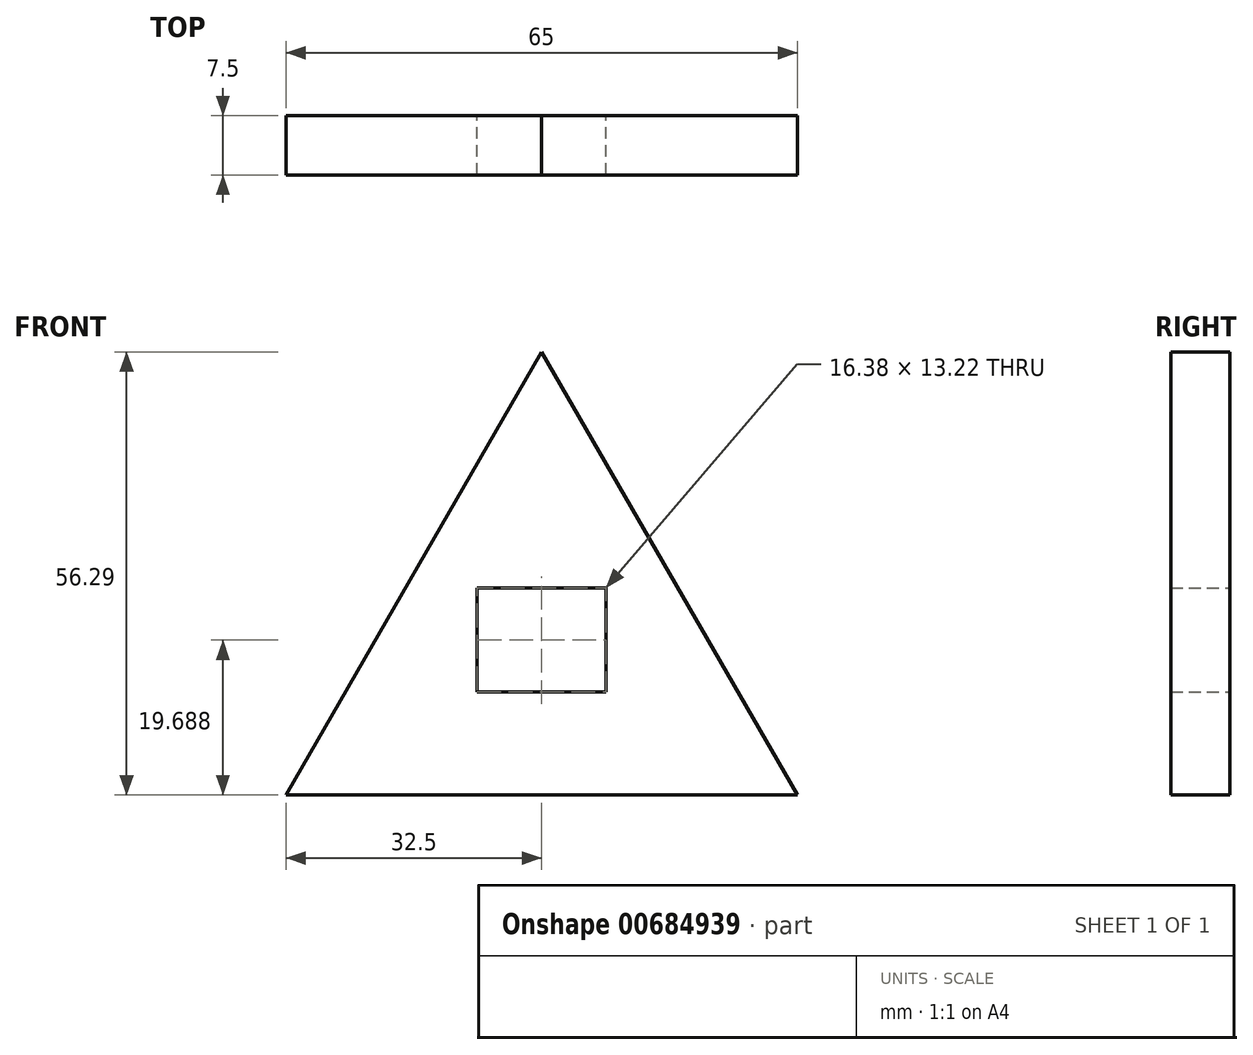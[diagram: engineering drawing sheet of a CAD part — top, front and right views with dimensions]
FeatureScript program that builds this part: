
annotation { "Feature Type Name" : "Feature", "Feature Type Description" : "" }
export const myFeature = defineFeature(function(context is Context, id is Id, definition is map)
    precondition{}
    {
        {
            var Q0;
            Q0=qCreatedBy(makeId("Front.planeOp"),FACE);
            var sketch = newSketch(context, id + "F0", { "sketchPlane" : qUnion([Q0])});
            skLineSegment(sketch, "E0", {"start": v(0, 56.3) * mm, "end": v(-32.5, 0) * mm});
            skLineSegment(sketch, "E1", {"start": v(-32.5, 0) * mm, "end": v(32.5, 0) * mm});
            skLineSegment(sketch, "E2", {"start": v(32.5, 0) * mm, "end": v(0, 56.3) * mm});
            skSolve(sketch);
        }
        {
            var Q0;
            Q0=makeQuery(id+"F0.imprint","IMPRINT",FACE,{"disambiguationData":[TD([[makeQuery(id+"F0.imprint","IMPRINT",EDGE,{"derivedFrom":sQuery(id+"F0.wireOp",EDGE,"E0")}),1.0]])]});
            extrude(context, id + "F1", {"entities" : qUnion([Q0]), "depth" : 7.5 * mm, "offsetDistance" : 25 * mm});
        }
        {
            var Q0;
            Q0=makeQuery(id+"F1.opExtrude","CAP_FACE",FACE,{"disambiguationData":[OSD([sQuery(id+"F0.wireOp",EDGE,"E0"),sQuery(id+"F0.wireOp",EDGE,"E1"),sQuery(id+"F0.wireOp",EDGE,"E2")])],"isStart":true});
            var sketch = newSketch(context, id + "F2", { "sketchPlane" : qUnion([Q0])});
            skLineSegment(sketch, "E3.bottom", {"start": v(-8.2, 13.08) * mm, "end": v(8.2, 13.08) * mm});
            skLineSegment(sketch, "E3.top", {"start": v(-8.2, 26.3) * mm, "end": v(8.2, 26.3) * mm});
            skLineSegment(sketch, "E3.left", {"start": v(-8.2, 13.08) * mm, "end": v(-8.2, 26.3) * mm});
            skLineSegment(sketch, "E3.right", {"start": v(8.2, 13.08) * mm, "end": v(8.2, 26.3) * mm});
            skPoint(sketch, "E3.middle", {"position": v(0, 19.69) * mm});
            skSolve(sketch);
        }
        {
            var Q0;
            Q0=makeQuery(id+"F2.imprint","IMPRINT",FACE,{"disambiguationData":[TD([[makeQuery(id+"F2.imprint","IMPRINT",EDGE,{"derivedFrom":sQuery(id+"F2.wireOp",EDGE,"E3.bottom")}),1.0]])]});
            extrude(context, id + "F3", {"entities" : qUnion([Q0]), "operationType" : NewBodyOperationType.REMOVE, "oppositeDirection" : true, "depth" : 25 * mm, "offsetDistance" : 25 * mm});
        }
    });
